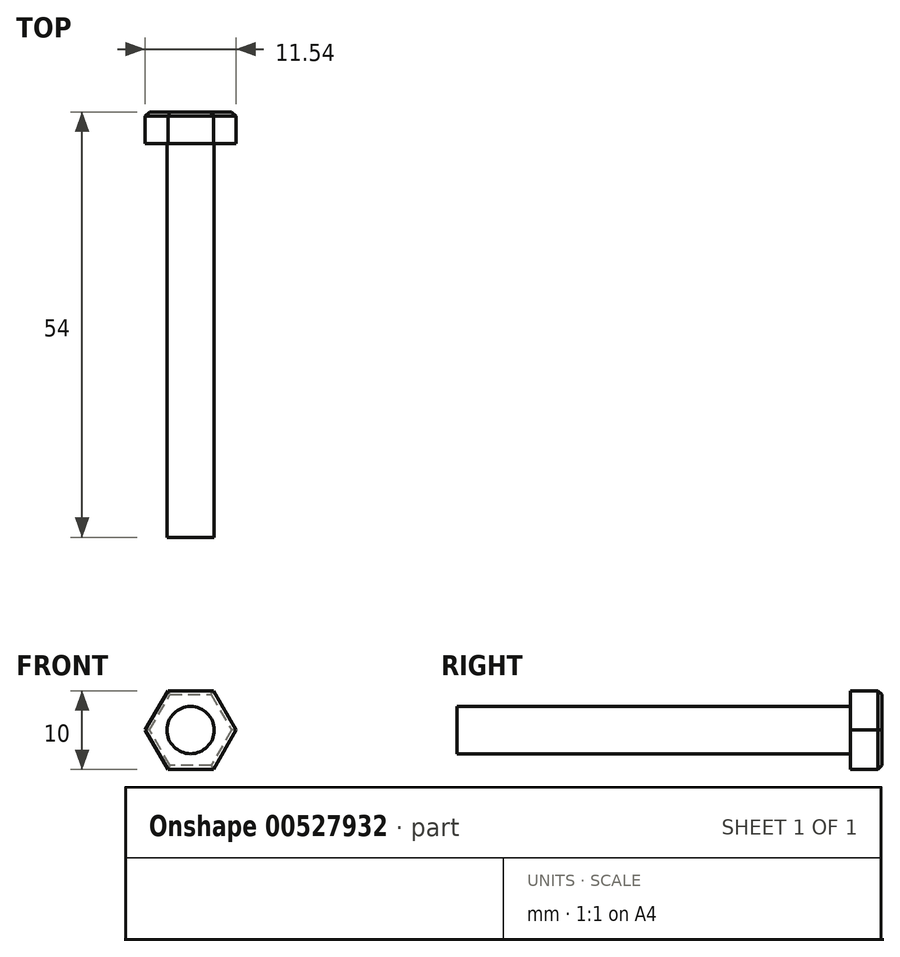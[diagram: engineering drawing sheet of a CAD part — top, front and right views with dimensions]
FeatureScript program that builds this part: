
annotation { "Feature Type Name" : "Feature", "Feature Type Description" : "" }
export const myFeature = defineFeature(function(context is Context, id is Id, definition is map)
    precondition{}
    {
        {
            var Q0;
            Q0=qCreatedBy(makeId("Front.planeOp"),FACE);
            var sketch = newSketch(context, id + "F0", { "sketchPlane" : qUnion([Q0])});
            skCircle(sketch, "E0.cCircle", {"center": v(0, 0) * mm, "radius": 5 * mm, "construction": true});
            skLineSegment(sketch, "E0.0", {"start": v(-2.89, 5) * mm, "end": v(2.89, 5) * mm});
            skLineSegment(sketch, "E0.1", {"start": v(2.89, 5) * mm, "end": v(5.77, 0) * mm});
            skLineSegment(sketch, "E0.2", {"start": v(5.77, 0) * mm, "end": v(2.89, -5) * mm});
            skLineSegment(sketch, "E0.3", {"start": v(2.89, -5) * mm, "end": v(-2.89, -5) * mm});
            skLineSegment(sketch, "E0.4", {"start": v(-2.89, -5) * mm, "end": v(-5.77, 0) * mm});
            skLineSegment(sketch, "E0.5", {"start": v(-5.77, 0) * mm, "end": v(-2.89, 5) * mm});
            skPoint(sketch, "E0.0.midPoint", {"position": v(0, 5) * mm});
            skSolve(sketch);
        }
        {
            var Q0;
            Q0=makeQuery(id+"F0.imprint","IMPRINT",FACE,{"disambiguationData":[TD([[makeQuery(id+"F0.imprint","IMPRINT",EDGE,{"derivedFrom":sQuery(id+"F0.wireOp",EDGE,"E0.0")}),-1.0]])]});
            extrude(context, id + "F1", {"entities" : qUnion([Q0]), "oppositeDirection" : true, "depth" : 4 * mm, "offsetDistance" : 25 * mm});
        }
        {
            var Q0;
            Q0=makeQuery(id+"F1.opExtrude","CAP_FACE",FACE,{"disambiguationData":[OSD([sQuery(id+"F0.wireOp",EDGE,"E0.0"),sQuery(id+"F0.wireOp",EDGE,"E0.1"),sQuery(id+"F0.wireOp",EDGE,"E0.2"),sQuery(id+"F0.wireOp",EDGE,"E0.3"),sQuery(id+"F0.wireOp",EDGE,"E0.4"),sQuery(id+"F0.wireOp",EDGE,"E0.5")])],"isStart":true});
            var sketch = newSketch(context, id + "F2", { "sketchPlane" : qUnion([Q0])});
            skCircle(sketch, "E1", {"center": v(0, 0) * mm, "radius": 3 * mm});
            skSolve(sketch);
        }
        {
            var Q0;
            Q0=makeQuery(id+"F2.imprint","IMPRINT",FACE,{"disambiguationData":[TD([[makeQuery(id+"F2.imprint","IMPRINT",EDGE,{"derivedFrom":sQuery(id+"F2.wireOp",EDGE,"E1")}),1.0]])]});
            extrude(context, id + "F3", {"entities" : qUnion([Q0]), "operationType" : NewBodyOperationType.ADD, "depth" : 50 * mm, "offsetDistance" : 25 * mm});
        }
        {
            var Q0;
            Q0=makeQuery(id+"F1.opExtrude","CAP_FACE",FACE,{"disambiguationData":[OSD([sQuery(id+"F0.wireOp",EDGE,"E0.0"),sQuery(id+"F0.wireOp",EDGE,"E0.1"),sQuery(id+"F0.wireOp",EDGE,"E0.2"),sQuery(id+"F0.wireOp",EDGE,"E0.3"),sQuery(id+"F0.wireOp",EDGE,"E0.4"),sQuery(id+"F0.wireOp",EDGE,"E0.5")])],"isStart":false});
            chamfer(context, id + "F4", {"entities" : qUnion([Q0]), "width" : 0.5 * mm, "tangentPropagation" : true});
        }
    });
